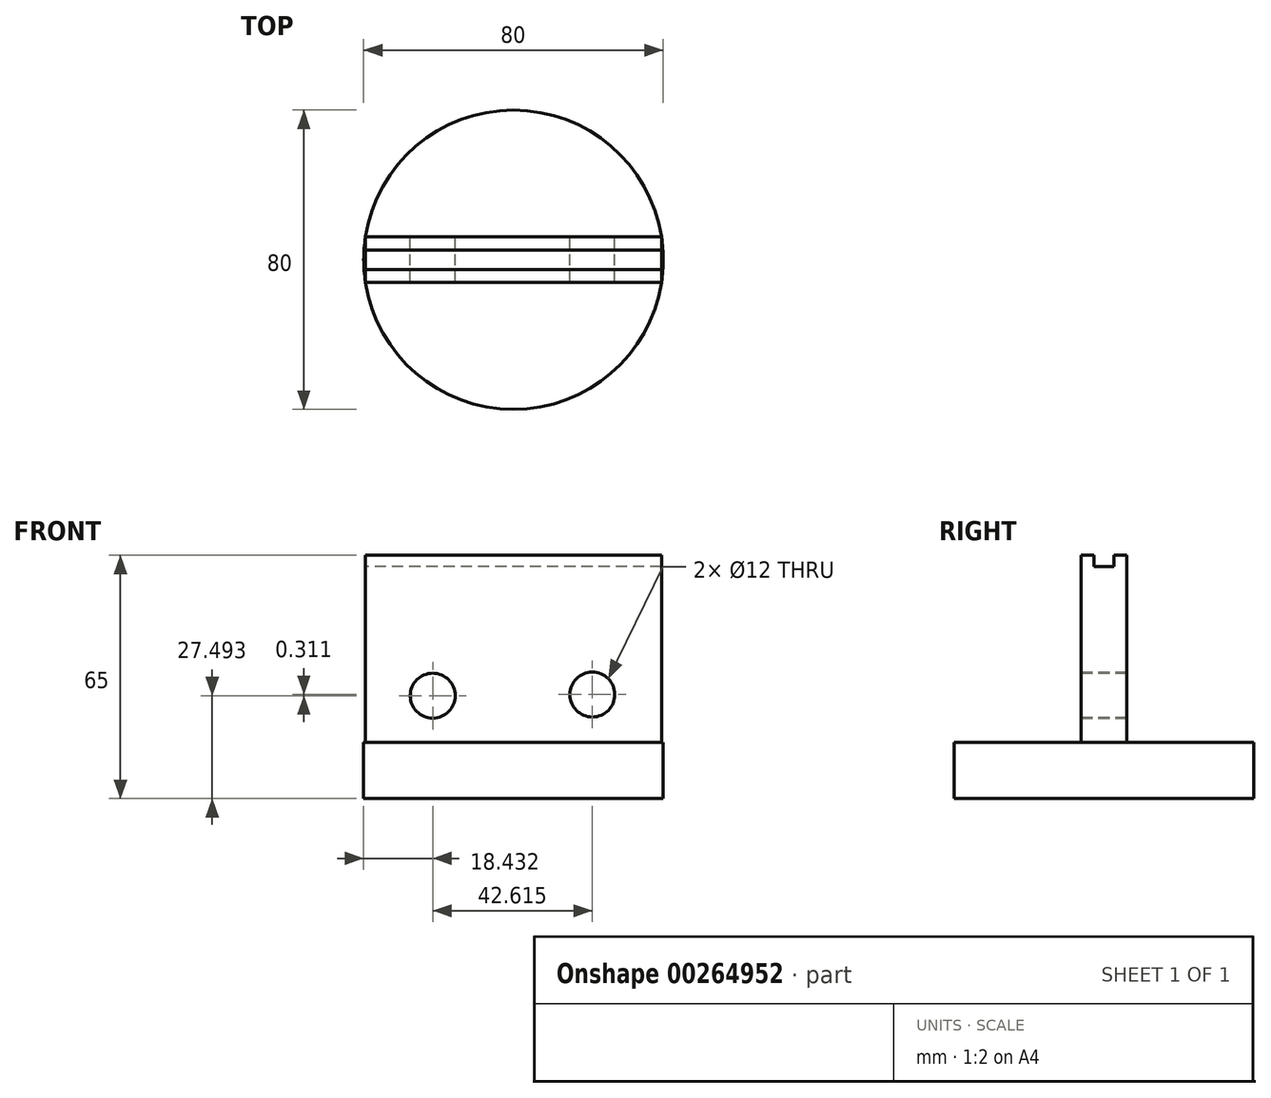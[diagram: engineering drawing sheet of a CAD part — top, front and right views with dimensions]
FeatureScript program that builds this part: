
annotation { "Feature Type Name" : "Feature", "Feature Type Description" : "" }
export const myFeature = defineFeature(function(context is Context, id is Id, definition is map)
    precondition{}
    {
        {
            var Q0;
            Q0=qCreatedBy(makeId("Top.planeOp"),FACE);
            var sketch = newSketch(context, id + "F0", { "sketchPlane" : qUnion([Q0])});
            skCircle(sketch, "E0", {"center": v(0, 0) * mm, "radius": 40 * mm});
            skSolve(sketch);
        }
        {
            var Q0;
            Q0=makeQuery(id+"F0.imprint","IMPRINT",FACE,{"disambiguationData":[TD([[makeQuery(id+"F0.imprint","IMPRINT",EDGE,{"derivedFrom":sQuery(id+"F0.wireOp",EDGE,"E0")}),1.0]])]});
            extrude(context, id + "F1", {"entities" : qUnion([Q0]), "depth" : 15 * mm});
        }
        {
            var Q0;
            Q0=makeQuery(id+"F1.opExtrude","CAP_FACE",FACE,{"disambiguationData":[OSD([sQuery(id+"F0.wireOp",EDGE,"E0")])],"isStart":false});
            var sketch = newSketch(context, id + "F2", { "sketchPlane" : qUnion([Q0])});
            skPoint(sketch, "E1.middle", {"position": v(0, 0) * mm});
            skLineSegment(sketch, "E2.bottom", {"start": v(39.53, -6.1) * mm, "end": v(-39.53, -6.1) * mm});
            skLineSegment(sketch, "E2.top", {"start": v(39.53, 6.1) * mm, "end": v(-39.53, 6.1) * mm});
            skLineSegment(sketch, "E2.left", {"start": v(39.53, -6.1) * mm, "end": v(39.53, 6.1) * mm});
            skLineSegment(sketch, "E2.right", {"start": v(-39.53, -6.1) * mm, "end": v(-39.53, 6.1) * mm});
            skSolve(sketch);
        }
        {
            var Q0;
            Q0=makeQuery(id+"F2.imprint","IMPRINT",FACE,{"disambiguationData":[TD([[makeQuery(id+"F2.imprint","IMPRINT",EDGE,{"derivedFrom":sQuery(id+"F2.wireOp",EDGE,"E2.bottom")}),-1.0]])]});
            extrude(context, id + "F3", {"entities" : qUnion([Q0]), "operationType" : NewBodyOperationType.ADD, "depth" : 50 * mm});
        }
        {
            var Q0;
            Q0=makeQuery(id+"F3.opExtrude","CAP_FACE",FACE,{"disambiguationData":[OSD([sQuery(id+"F2.wireOp",EDGE,"E2.bottom"),sQuery(id+"F2.wireOp",EDGE,"E2.top"),sQuery(id+"F2.wireOp",EDGE,"E2.left"),sQuery(id+"F2.wireOp",EDGE,"E2.right")])],"isStart":false});
            var sketch = newSketch(context, id + "F4", { "sketchPlane" : qUnion([Q0])});
            skLineSegment(sketch, "E3.bottom", {"start": v(39.53, -2.64) * mm, "end": v(-39.53, -2.64) * mm});
            skLineSegment(sketch, "E3.top", {"start": v(39.53, 2.64) * mm, "end": v(-39.53, 2.64) * mm});
            skLineSegment(sketch, "E3.left", {"start": v(39.53, -2.64) * mm, "end": v(39.53, 2.64) * mm});
            skLineSegment(sketch, "E3.right", {"start": v(-39.53, -2.64) * mm, "end": v(-39.53, 2.64) * mm});
            skPoint(sketch, "E3.middle", {"position": v(0, 0) * mm});
            skSolve(sketch);
        }
        {
            var Q0;
            Q0 = qSketchRegion(id + "F4", true);
            extrude(context, id + "F5", {"entities" : qUnion([Q0]), "operationType" : NewBodyOperationType.REMOVE, "oppositeDirection" : true, "depth" : 3 * mm});
        }
        {
            var Q0;
            Q0=makeQuery(id+"F3.opExtrude","SWEPT_FACE",FACE,{"disambiguationData":[OSD([sQuery(id+"F2.wireOp",EDGE,"E2.top")])]});
            var sketch = newSketch(context, id + "F6", { "sketchPlane" : qUnion([Q0])});
            skCircle(sketch, "E4", {"center": v(-21.05, 27.8) * mm, "radius": 6 * mm});
            skCircle(sketch, "E5", {"center": v(21.57, 27.5) * mm, "radius": 6 * mm});
            skSolve(sketch);
        }
        {
            var Q0;
            Q0 = qSketchRegion(id + "F6", true);
            extrude(context, id + "F7", {"entities" : qUnion([Q0]), "operationType" : NewBodyOperationType.REMOVE, "oppositeDirection" : true, "depth" : 25 * mm});
        }
    });
